# Revit family: Plumbing_Drainage_hansgrohe_56223XXX-RainDrain-Minimalistic-Finish-s__
name_source: partatom
category: Plumbing Fixtures
revit_build: Autodesk Revit 2018 (Build: 20170223_1515(x64)
units: mm (PartAtom-declared; Revit-internal decimal feet)

## family parameters
Cut with Voids When Loaded = No
Host = Face
OmniClass Number = 23.31.17.29
OmniClass Title = Shower Drains
Part Type = Normal
Room Calculation Point = No
Round Connector Dimension = Use Diameter
Shared = No

## types (1)
- 56223XXX RainDrain Minimalistic Finish set shower drain 1200
    Default Elevation = 1219 mm
    Description = RainDrain Minimalistic Finish set shower drain 1200
    Edition number = 0
    Manufacturer = Hansgrohe
    Material = Hansgrohe - Metal - Stainless Steel
    Material 1 = Hansgrohe - Plastic - Black
    Model = 56223XXX
    Product Guid = 0a96f6e4-5ac7-4ec5-ac56-1429f9f7e5ed
    Product Page URL = https://pro.hansgrohe.com
    Product data url = https://bimobject.com
    URL = https://www.hansgrohe.com
    Version = 1

## geometry (parser evidence)
native form markers: Sweep x5
no freeform markers — native parametric forms only
